# Revit family: 600x600
name_source: partatom
category: Lighting Fixtures
revit_build: Autodesk Revit 2017 (Build: 20190507_1515(x64)
units: mm (PartAtom-declared; Revit-internal decimal feet)

## family parameters
Cut with Voids When Loaded = No
Host = Face
Light Source = Yes
OmniClass Number = 23.80.70.00
OmniClass Title = Lighting
Part Type = Normal
Room Calculation Point = No
Round Connector Dimension = Use Diameter
Shared = No

## types (2) — shared parameters
-LUMDEPTH_SYL = -277 mm
Apparent Load = 34 VA
Assembly Code = D5020200
AssetType = Fixed
BOX_WIDTH_SYL = 40 mm  [stored 0.131234 ft]
ClassificationName = Uniclass2015
ClassificationValue = EF_70_80
Color Filter = 16777215
DEPTH_SYL = 298 mm
Default Elevation = 1219 mm
Dimming Lamp Color Temperature Shift = <None>
DocumentationLiterature = http://www.sylvania-lighting.com
ElectricShockClassification = Class II
Emit Shape Visible in Rendering = No
Emit from Circle Diameter = 610 mm
HEIGHTBOTT_SYL = 7 mm  [stored 0.0229659 ft]
HEIGHT_SYL = 33 mm  [stored 0.108268 ft]
IfcExportAs = IfcLightFixtureType
IfcExportType = IfcLightFixtureType
ImpactProtectionIndex = IK03
IngressProtection = IP44/20
Keynote = 16500
LUMDEPTH_SYL = 277 mm
LUMWIDTH_SYL = 277 mm
Lamp = LED
LampColourRenderingIndex = 80
LampMacAdamStep = 3
LampsType = LED
MAINHEIGHT_SYL = 63 mm
Manufacturer = Feilo Sylvania
ManufacturerName = Feilo Sylvania
Material = aluminium,steel housing, other diffuser
Material_1_SYL = Default
Material_2_SYL = <By Category>
Material_3_SYL = <By Category>
Material_4_SYL = <By Category>
NominalDepth = 595 mm
NominalHeight = 35 mm
NominalLength = 595 mm
PowerConsumption = 34 W
TOPWIDTH_SYL = 245 mm  [stored 0.803806 ft]
Tilt Angle = -90.00°
Type Image = <None>
URL = http://www.sylvania-lighting.com
Voltage = 0 V
WIDTH_SYL = 298 mm
Weight = 7.2 kg
zero-valued in all types: Cost, PowerFactor

## per-type parameters (varying)
| type | LampColourTemperature | LampNominalLuminous | LuminousEfficacy | Model | ModelNumber | ModelReference | Name | Photometric Web File | TypeName |
| 0042639 S PL U19 600HE IP44 DALI 4300 840 TPA | 4000 K | 4300 lm | 126 lm/W | ST Panel UGR19 600x600 HE IP44 DALI 4300 840 TPA | 0042639 | ST Panel UGR19 600x600 HE IP44 DALI 4300 840 TPA | ST Panel UGR19 600x600 HE IP44 DALI 4300 840 TPA | 0042639.ies | ST Panel UGR19 600x600 HE IP44 DALI 4300 840 TPA |
| 0042638 S PL U19 600HE IP44 DALI 4100 830 TPA | 3000 K | 4100 lm | 121 lm/W | ST Panel UGR19 600x600 HE IP44 DALI 4100 830 TPA | 0042638 | ST Panel UGR19 600x600 HE IP44 DALI 4100 830 TPA | ST Panel UGR19 600x600 HE IP44 DALI 4100 830 TPA | 0042638.ies | ST Panel UGR19 600x600 HE IP44 DALI 4100 830 TPA |

note: [stored X ft] marks values corroborated as IEEE doubles in the binary element streams (Revit-internal decimal feet)

## geometry (parser evidence)
native form markers: Sweep x2
no freeform markers — native parametric forms only
